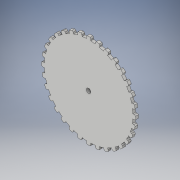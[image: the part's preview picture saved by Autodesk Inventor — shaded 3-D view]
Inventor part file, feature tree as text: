
AUTODESK INVENTOR PART (.ipt)
format: ipt  version: 2017 (Build 210142000, 142)  size: 339,968 bytes
history: native  units: in
note: dims shown in document units (in); Inventor stores cm internally (conversion verified against a paired STEP export)
features: extrude x2, sketch x2, pattern_circular x1
ambient origin geometry x8: Origin, YZ Plane, XZ Plane, XY Plane, X Axis, Y Axis, Z Axis, Center Point
bodies: Body1 (feature_tree)
feature tree (5):
  extrude  "Extrusion2"  Depth=0.075in
  pattern_circular  "Circular Pattern2"  Count=128 Angle=360.0deg
  extrude  "Extrusion3"  Depth=0.075in TaperAngle=0.0deg
  sketch  "Sketch1"  dims[d0=2.4in d10=0.075in]
  sketch  "Sketch2"  dims[d11=0.04in d12=50.3937in d14=360.0deg d16=0.075in d17=0.0in d18=12.5984in d19=360.0deg d21=0.122in d22=1.0in d23=0.0in]
